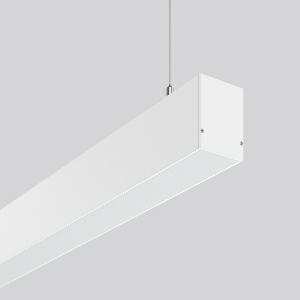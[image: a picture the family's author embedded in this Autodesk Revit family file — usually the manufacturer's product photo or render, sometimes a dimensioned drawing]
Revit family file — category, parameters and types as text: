
# Revit family: less_is_more_50_312319_002_88c6
name_source: partatom
category: Lighting Fixtures
units: mm (PartAtom-declared; Revit-internal decimal feet)

## family parameters
Cut with Voids When Loaded = No
Host = Face
Light Source = No
Part Type = Normal
Room Calculation Point = No
Round Connector Dimension = Use Diameter
Shared = No

## types (1)
- LESS IS MORE 50 (1 x LED Modul 830, 6150 lm, 3000)
    Apparent Load = 52 VA
    CIE Flux Codes = 49 80 96 63 100
    Color Rendering = 80
    Color Temperature = 3000
    Default Elevation = 1800 mm
    Description = Series: LESS IS MORE 50
Linear pendant luminaire for aesthetically sophisticated lighting. Housing: extruded aluminium profile, powder-coated. End cap aluminium powder-coated. Canopy made of aluminium, powder-coated. Diffuser made of non-yellowing plastic (PMMA), opal. Direct 65%, indirect 35% light emission. Suitable for pendant. 2-point steel cable suspension freely positionable and infinitely height-adjustable. Special lengths available on request. LED unit with integrated converter interchangeable and removable. Suitable for through-wiring. With sensors or as a safety luminaire on request. 
Colour: traffic white, matt (RAL 9016)
Length: 1407 mm
Width: 57 mm
Height: 75 mm
Suspension length: 2000 mm
Lamp: LED
Socket: without socket
Colour temperature: 3000K
Colour rendering index (CRI): 80
Light source: LED
Socket lamp2: Without base
Colour temperature: 3000K
System power: 52 W
Rated luminous flux: 6150 lm
Luminous efficiency: 118 lm/W
Control gear: Regulated power supply
Control gear: Regulated power supply
Protection class: I
Type of protection: IP 20
    Height = 75 mm
    Lamp = 1 x LED Modul 830
    Lamp Light Flux = 6150 lm
    Lamp count = 1
    Length = 1407 mm
    Lifetime = 50000 h
    Luminous efficacy = 118 lm/W
    Manufacturer = RZB
    ModVariant = No
    Model = 312319.002
    Mounting Place = Ceiling
    Mounting Type = Pendant
    Number of Poles = 1
    OnlyDefault = Yes
    Power Factor = 1
    Product Name = LESS IS MORE 50
    Product group = Pendant LED linear luminaires
    ProductGroupID = 907
    Protection Class = Protection class I
    Protection Degree = IP 20
    RLX_Detail_Level = 1
    RLX_Emergency_Light_Flux = 0 lm
    RLX_Emergency_Type = 0
    RLX_Emergency_Type_DB = No
    RlxData = <blob elided: 31625 chars, md5=f7b41455>
    Socket = socket
    Standby Power = 0 W
    System Light Flux = 6150 lm
    System Power = 52 W
    Type Comments = Product without accessories
    Type Image = 312318.002.jpg
    URL = http://relux.com
    VarID = ---
    Voltage = 230 V
    Voltage Range = 220-240 V
    Weight = 0.00 kg
    Width = 57 mm

## geometry (parser evidence)
native form markers: Blend x4, Sweep x12
no freeform markers — native parametric forms only
